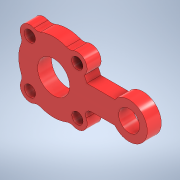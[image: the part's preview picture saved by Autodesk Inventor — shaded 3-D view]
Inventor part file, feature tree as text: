
AUTODESK INVENTOR PART (.ipt)
format: ipt  version: 2021 (Build 250183000, 183)  size: 175,104 bytes
history: native  units: in
note: dims shown in document units (in); Inventor stores cm internally (conversion verified against a paired STEP export)
features: sketch x2, extrude x2, fillet x2
ambient origin geometry x8: Origin, YZ Plane, XZ Plane, XY Plane, X Axis, Y Axis, Z Axis, Center Point
bodies: Solid1 (feature_tree)
feature tree (6):
  sketch  "Sketch1"  dims[d1=0.9055in d2=1.8898in]
  sketch  "Sketch2"  dims[d3=1.9685in d4=0.315in d5=0.5512in d6=1.5748in d8=360.0deg d10=2.126in d11=0.5906in d12=1.0236in d13=0.315in d14=0.6299in d15=0.3937in d16=0.0in d17=0.3937in d18=0.0in d19=0.1575in d20=0.2362in]
  extrude  "Extrusion1"  Depth=1.8898in
  extrude  "Extrusion2"  Depth=0.2362in
  fillet  "Fillet1"  Radius=0.5512in
  fillet  "Fillet2"  Radius=1.5748in
